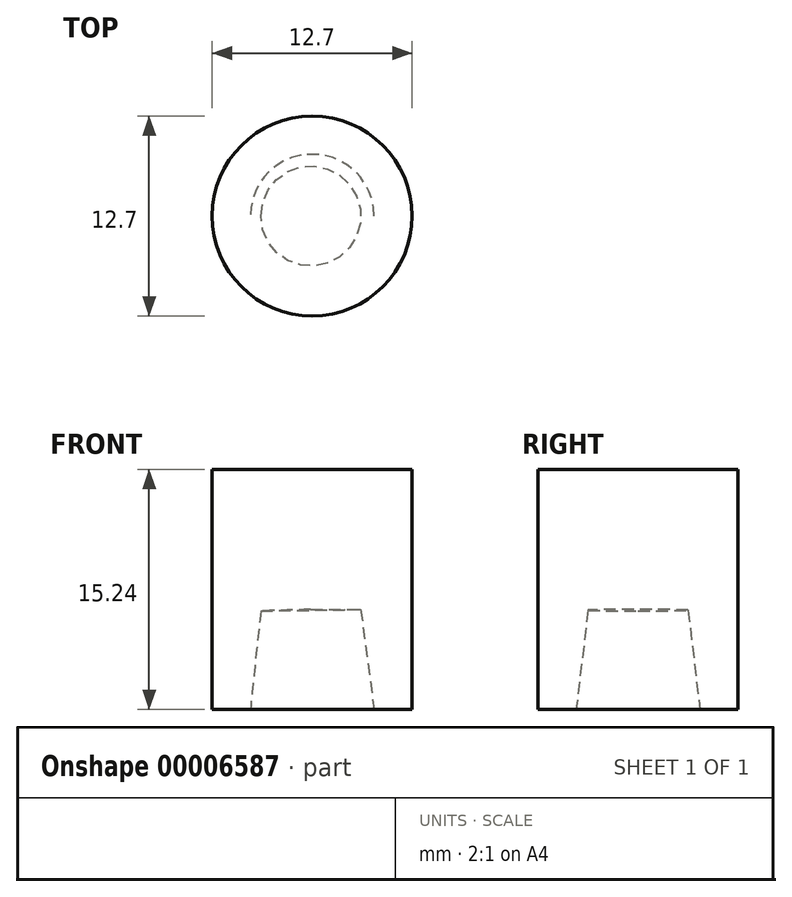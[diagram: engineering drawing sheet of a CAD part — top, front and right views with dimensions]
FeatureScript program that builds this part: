
annotation { "Feature Type Name" : "Feature", "Feature Type Description" : "" }
export const myFeature = defineFeature(function(context is Context, id is Id, definition is map)
    precondition{}
    {
        {
            var Q0;
            Q0=qCreatedBy(makeId("Front.planeOp"),FACE);
            var sketch = newSketch(context, id + "F0", { "sketchPlane" : qUnion([Q0])});
            skLineSegment(sketch, "E0", {"start": v(-0.09, 6.35) * mm, "end": v(3.09, 6.35) * mm});
            skLineSegment(sketch, "E1", {"start": v(3.09, 6.35) * mm, "end": v(3.94, 0) * mm});
            skLineSegment(sketch, "E2", {"start": v(3.94, 0) * mm, "end": v(0, 0) * mm});
            skLineSegment(sketch, "E3", {"start": v(0, 0) * mm, "end": v(-0.09, 6.35) * mm});
            skSolve(sketch);
        }
        {
            var Q0;
            Q0=qCreatedBy(makeId("Top.planeOp"),FACE);
            var sketch = newSketch(context, id + "F1", { "sketchPlane" : qUnion([Q0])});
            skCircle(sketch, "E4", {"center": v(0, 0) * mm, "radius": 6.35 * mm});
            skSolve(sketch);
        }
        {
            var Q0;
            Q0=qSketchRegion(id+"F1",true);
            extrude(context, id + "F2", {"entities" : qUnion([Q0]), "depth" : 15.24 * mm});
        }
        {
            var Q0;
            Q0=makeQuery(id+"F0.imprint","IMPRINT",FACE,{"disambiguationData":[TD([[makeQuery(id+"F0.imprint","IMPRINT",EDGE,{"derivedFrom":sQuery(id+"F0.wireOp",EDGE,"E0")}),-1.0]])]});
            var Q1;
            Q1=sQuery(id+"F0.wireOp",EDGE,"E3");
            revolve(context, id + "F3", {"operationType" : NewBodyOperationType.REMOVE, "entities" : qUnion([Q0]), "axis" : qUnion([Q1]), "revolveType" : RevolveType.FULL});
        }
    });
